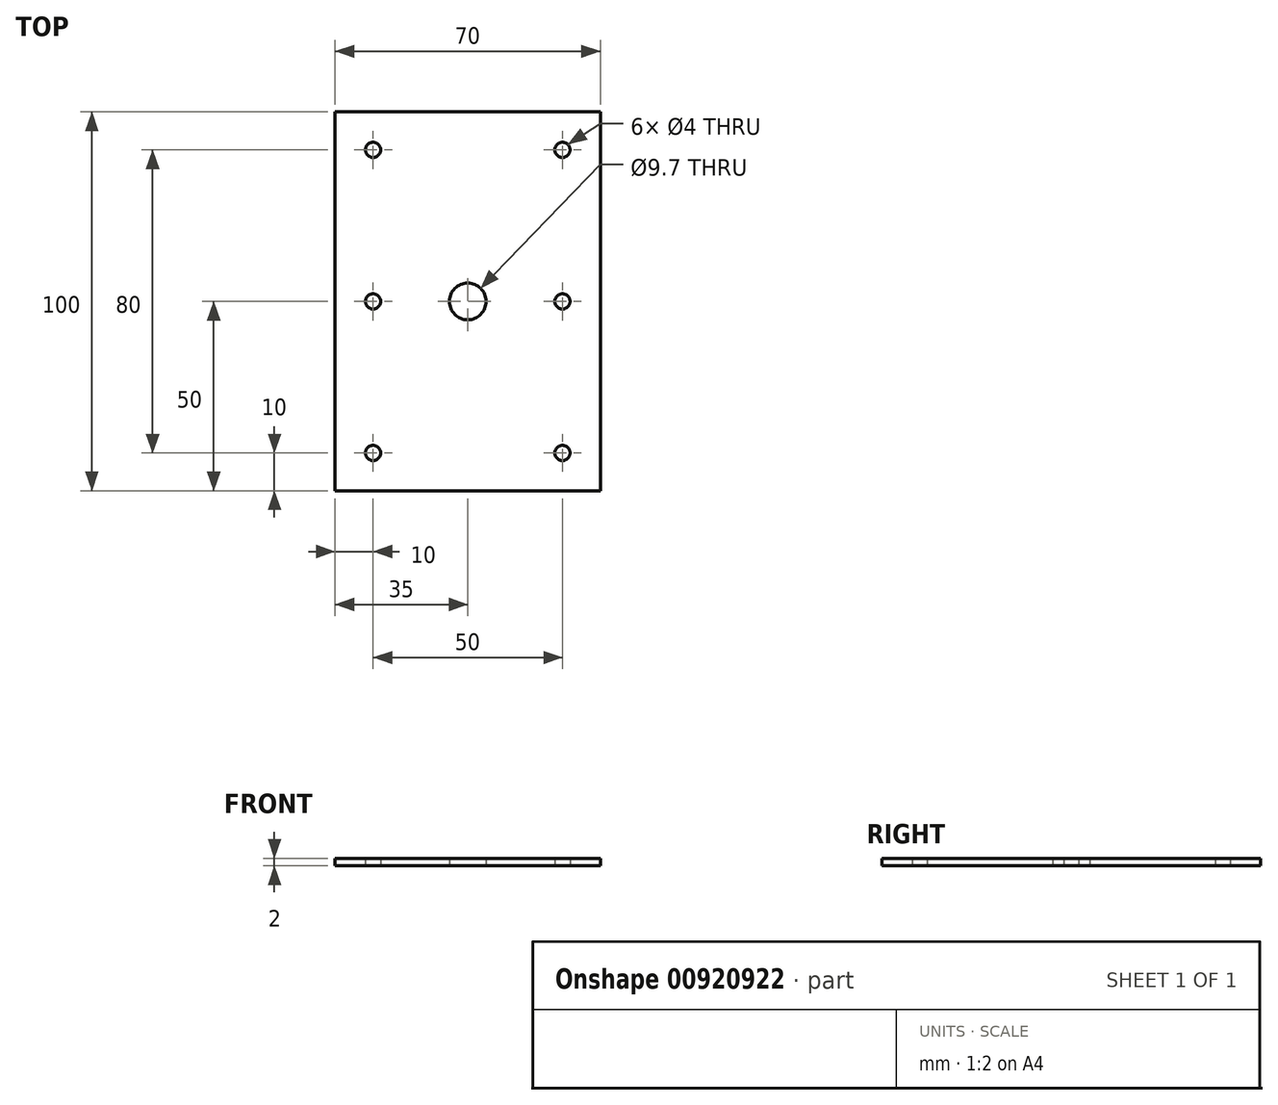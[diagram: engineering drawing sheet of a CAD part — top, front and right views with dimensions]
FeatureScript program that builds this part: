
annotation { "Feature Type Name" : "Feature", "Feature Type Description" : "" }
export const myFeature = defineFeature(function(context is Context, id is Id, definition is map)
    precondition{}
    {
        {
            var Q0;
            Q0=qCreatedBy(makeId("Top.planeOp"),FACE);
            var sketch = newSketch(context, id + "F0", { "sketchPlane" : qUnion([Q0])});
            skCircle(sketch, "E0", {"center": v(0, 0) * mm, "radius": 4.85 * mm});
            skLineSegment(sketch, "E1", {"start": v(-20, 0) * mm, "end": v(20, 0) * mm});
            skCircle(sketch, "E2", {"center": v(-25, 0) * mm, "radius": 2 * mm});
            skCircle(sketch, "E3", {"center": v(25, 0) * mm, "radius": 2 * mm});
            skLineSegment(sketch, "E4.bottom", {"start": v(-35, 50) * mm, "end": v(35, 50) * mm});
            skLineSegment(sketch, "E4.top", {"start": v(-35, -50) * mm, "end": v(35, -50) * mm});
            skLineSegment(sketch, "E4.left", {"start": v(-35, 50) * mm, "end": v(-35, -50) * mm});
            skLineSegment(sketch, "E4.right", {"start": v(35, 50) * mm, "end": v(35, -50) * mm});
            skCircle(sketch, "E5", {"center": v(-25, 40) * mm, "radius": 2 * mm});
            skCircle(sketch, "E6", {"center": v(-25, -40) * mm, "radius": 2 * mm});
            skCircle(sketch, "E7", {"center": v(25, -40) * mm, "radius": 2 * mm});
            skCircle(sketch, "E8", {"center": v(25, 40) * mm, "radius": 2 * mm});
            skSolve(sketch);
        }
        {
            var Q0;
            Q0=qSketchRegion(id+"F0",true);
            extrude(context, id + "F1", {"entities" : qUnion([Q0]), "depth" : 2 * mm, "offsetDistance" : 25 * mm});
        }
    });
